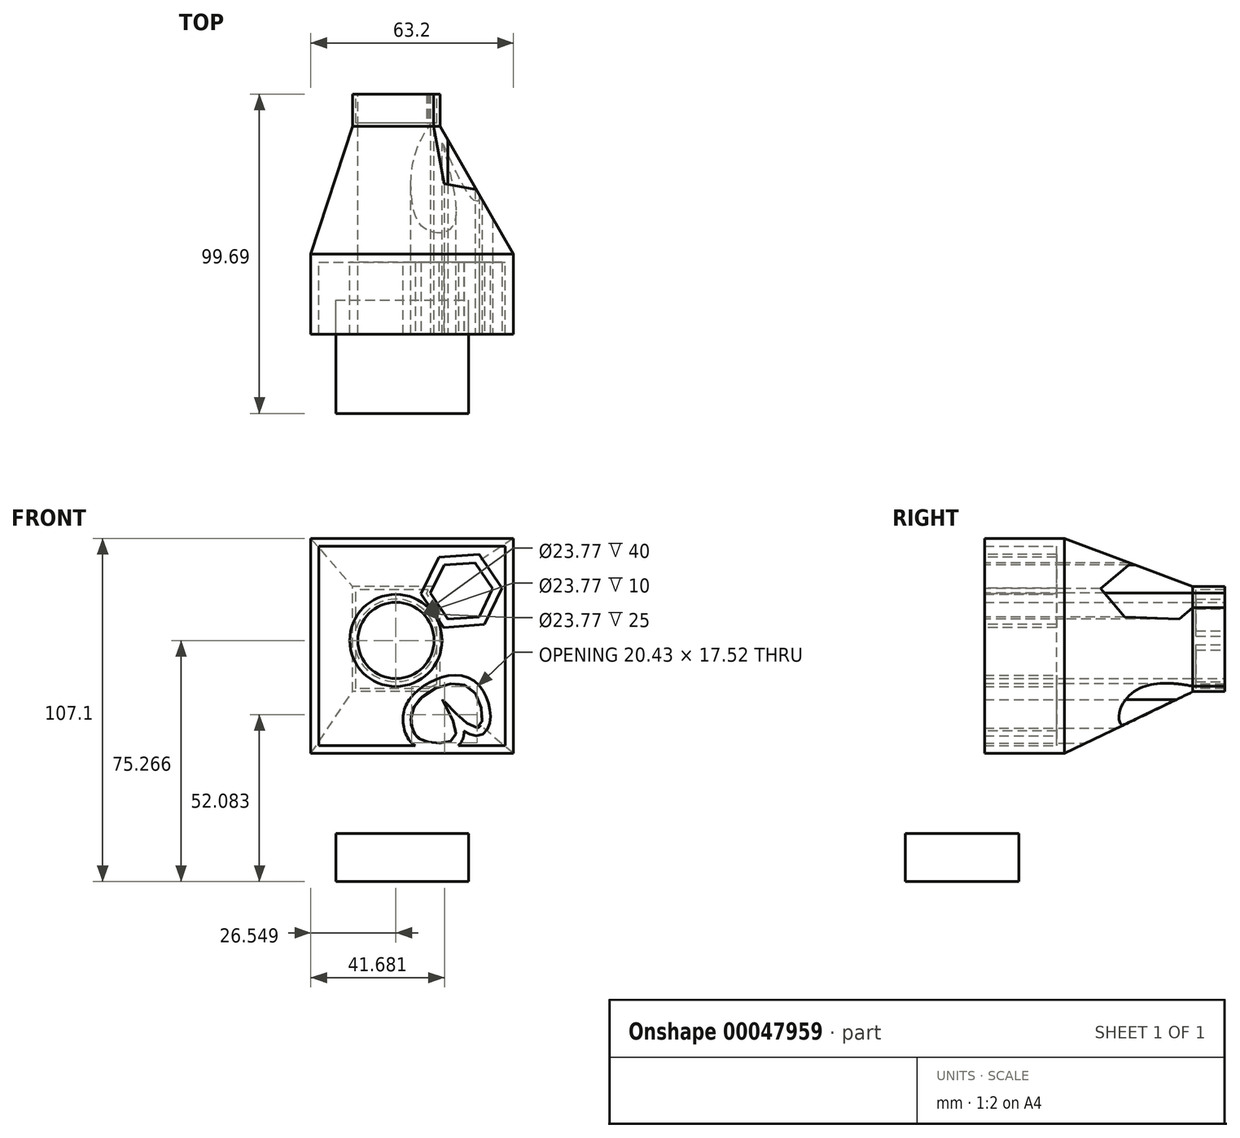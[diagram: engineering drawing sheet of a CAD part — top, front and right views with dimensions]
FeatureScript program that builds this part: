
annotation { "Feature Type Name" : "Feature", "Feature Type Description" : "" }
export const myFeature = defineFeature(function(context is Context, id is Id, definition is map)
    precondition{}
    {
        {
            var Q0;
            Q0=qCreatedBy(makeId("Front.planeOp"),FACE);
            var sketch = newSketch(context, id + "F0", { "sketchPlane" : qUnion([Q0])});
            skLineSegment(sketch, "E0.bottom", {"start": v(0, 0) * mm, "end": v(63.2, 0) * mm});
            skLineSegment(sketch, "E0.top", {"start": v(0, 67.1) * mm, "end": v(63.2, 67.1) * mm});
            skLineSegment(sketch, "E0.right", {"start": v(63.2, 0) * mm, "end": v(63.2, 67.1) * mm});
            skLineSegment(sketch, "E1", {"start": v(0, 67.1) * mm, "end": v(0, 0) * mm});
            skSolve(sketch);
        }
        {
            var Q0;
            Q0=makeQuery(id+"F0.imprint","IMPRINT",FACE,{"disambiguationData":[TD([[makeQuery(id+"F0.imprint","IMPRINT",EDGE,{"derivedFrom":sQuery(id+"F0.wireOp",EDGE,"E0.bottom")}),1.0]])]});
            extrude(context, id + "F1", {"entities" : qUnion([Q0]), "depth" : 25 * mm});
        }
        {
            var Q0;
            Q0=qCreatedBy(makeId("Front.planeOp"),FACE);
            cPlane(context, id + "F2", {"entities" : qUnion([Q0]), "cplaneType" : CPlaneType.OFFSET, "offset" : 50 * mm, "oppositeDirection" : true, "width" : 150 * mm, "height" : 150 * mm});
        }
        {
            var Q0;
            Q0=qCreatedBy(id+"F2.planeOp",FACE);
            var sketch = newSketch(context, id + "F3", { "sketchPlane" : qUnion([Q0])});
            skLineSegment(sketch, "E2.bottom", {"start": v(40.36, 19.28) * mm, "end": v(13, 19.28) * mm});
            skLineSegment(sketch, "E2.top", {"start": v(40.36, 52.07) * mm, "end": v(13, 52.07) * mm});
            skLineSegment(sketch, "E2.right", {"start": v(13, 19.28) * mm, "end": v(13, 52.07) * mm});
            skLineSegment(sketch, "E3", {"start": v(40.36, 19.28) * mm, "end": v(40.36, 52.07) * mm});
            skSolve(sketch);
        }
        {
            var Q0;
            Q0=makeQuery(id+"F3.imprint","IMPRINT",FACE,{"disambiguationData":[TD([[makeQuery(id+"F3.imprint","IMPRINT",EDGE,{"derivedFrom":sQuery(id+"F3.wireOp",EDGE,"E2.bottom")}),-1.0]])]});
            extrude(context, id + "F4", {"entities" : qUnion([Q0]), "depth" : 10 * mm});
        }
        {
            var Q0;
            Q0=makeQuery(id+"F1.opExtrude","CAP_FACE",FACE,{"disambiguationData":[OSD([sQuery(id+"F0.wireOp",EDGE,"E0.bottom"),sQuery(id+"F0.wireOp",EDGE,"E0.top"),sQuery(id+"F0.wireOp",EDGE,"E0.right"),sQuery(id+"F0.wireOp",EDGE,"E1")])],"isStart":true});
            var Q1;
            Q1=makeQuery(id+"F4.opExtrude","CAP_FACE",FACE,{"disambiguationData":[OSD([sQuery(id+"F3.wireOp",EDGE,"E2.bottom"),sQuery(id+"F3.wireOp",EDGE,"E2.top"),sQuery(id+"F3.wireOp",EDGE,"E2.right"),sQuery(id+"F3.wireOp",EDGE,"E3")])],"isStart":false});
            loft(context, id + "F5", {"sheetProfilesArray" : [{ "sheetProfileEntities" : qUnion([Q0]) }, { "sheetProfileEntities" : qUnion([Q1]) }]});
        }
        {
            var Q0;
            Q0=makeQuery(id+"F4.opExtrude","CAP_FACE",FACE,{"disambiguationData":[OSD([sQuery(id+"F3.wireOp",EDGE,"E2.bottom"),sQuery(id+"F3.wireOp",EDGE,"E2.top"),sQuery(id+"F3.wireOp",EDGE,"E2.right"),sQuery(id+"F3.wireOp",EDGE,"E3")])],"isStart":true});
            var sketch = newSketch(context, id + "F6", { "sketchPlane" : qUnion([Q0])});
            skCircle(sketch, "E4", {"center": v(-26.55, 35.27) * mm, "radius": 11.89 * mm});
            skSolve(sketch);
        }
        {
            var Q0;
            Q0=makeQuery(id+"F6.imprint","IMPRINT",FACE,{"disambiguationData":[TD([[makeQuery(id+"F6.imprint","IMPRINT",EDGE,{"derivedFrom":sQuery(id+"F6.wireOp",EDGE,"E4")}),1.0]])]});
            extrude(context, id + "F7", {"entities" : qUnion([Q0]), "operationType" : NewBodyOperationType.REMOVE, "oppositeDirection" : true, "depth" : 200 * mm});
        }
        {
            var Q0;
            Q0=makeQuery(id+"F1.opExtrude","CAP_FACE",FACE,{"disambiguationData":[OSD([sQuery(id+"F0.wireOp",EDGE,"E0.bottom"),sQuery(id+"F0.wireOp",EDGE,"E0.top"),sQuery(id+"F0.wireOp",EDGE,"E0.right"),sQuery(id+"F0.wireOp",EDGE,"E1")])],"isStart":false});
            var sketch = newSketch(context, id + "F8", { "sketchPlane" : qUnion([Q0])});
            skCircle(sketch, "E5.cCircle", {"center": v(47.04, 50.7) * mm, "radius": 8.47 * mm, "construction": true});
            skLineSegment(sketch, "E5.0", {"start": v(51.3, 59.5) * mm, "end": v(56.79, 51.41) * mm});
            skLineSegment(sketch, "E5.1", {"start": v(56.79, 51.41) * mm, "end": v(52.52, 42.62) * mm});
            skLineSegment(sketch, "E5.2", {"start": v(52.52, 42.62) * mm, "end": v(42.77, 41.91) * mm});
            skLineSegment(sketch, "E5.3", {"start": v(42.77, 41.91) * mm, "end": v(37.28, 50) * mm});
            skLineSegment(sketch, "E5.4", {"start": v(37.28, 50) * mm, "end": v(41.55, 58.8) * mm});
            skLineSegment(sketch, "E5.5", {"start": v(41.55, 58.8) * mm, "end": v(51.3, 59.5) * mm});
            skPoint(sketch, "E5.0.midPoint", {"position": v(54.05, 55.46) * mm});
            skFitSpline(sketch, "E6", {"points": [v(51.9, 7.97) * mm, v(49.75, 20.4) * mm, v(32.9, 15.55) * mm, v(32.11, 6.73) * mm, v(36.3, 3.67) * mm, v(45.23, 5.82) * mm, v(41.04, 16.8) * mm, v(51.9, 7.97) * mm]});
            skSolve(sketch);
        }
        {
            var Q0;
            Q0=makeQuery(id+"F8.imprint","IMPRINT",FACE,{"disambiguationData":[TD([[makeQuery(id+"F8.imprint","IMPRINT",EDGE,{"derivedFrom":sQuery(id+"F8.wireOp",EDGE,"E5.0")}),-1.0]])]});
            var Q1;
            Q1=makeQuery(id+"F8.imprint","IMPRINT",FACE,{"disambiguationData":[TD([[makeQuery(id+"F8.imprint","IMPRINT",EDGE,{"derivedFrom":sQuery(id+"F8.wireOp",EDGE,"E6")}),1.0]])]});
            extrude(context, id + "F9", {"entities" : qUnion([Q0, Q1]), "operationType" : NewBodyOperationType.REMOVE, "oppositeDirection" : true, "depth" : 200 * mm});
        }
        {
            var Q0;
            Q0=makeQuery(id+"F1.opExtrude","CAP_FACE",FACE,{"disambiguationData":[OSD([sQuery(id+"F0.wireOp",EDGE,"E0.bottom"),sQuery(id+"F0.wireOp",EDGE,"E0.top"),sQuery(id+"F0.wireOp",EDGE,"E0.right"),sQuery(id+"F0.wireOp",EDGE,"E1")])],"isStart":false});
            shell(context, id + "F10", {"entities" : qUnion([Q0]), "thickness" : 2.5 * mm});
        }
        {
            var Q0;
            Q0=makeQuery(id+"F4.opExtrude","CAP_FACE",FACE,{"disambiguationData":[OSD([sQuery(id+"F3.wireOp",EDGE,"E2.bottom"),sQuery(id+"F3.wireOp",EDGE,"E2.top"),sQuery(id+"F3.wireOp",EDGE,"E2.right"),sQuery(id+"F3.wireOp",EDGE,"E3")])],"isStart":true});
            shell(context, id + "F11", {"entities" : qUnion([Q0]), "thickness" : 1 * mm});
        }
        {
            var Q0;
            Q0=qCreatedBy(makeId("Top.planeOp"),FACE);
            cPlane(context, id + "F12", {"entities" : qUnion([Q0]), "cplaneType" : CPlaneType.OFFSET, "offset" : 40 * mm, "oppositeDirection" : true, "width" : 150 * mm, "height" : 150 * mm});
        }
        {
            var Q0;
            Q0=qCreatedBy(id+"F12.planeOp",FACE);
            var sketch = newSketch(context, id + "F13", { "sketchPlane" : qUnion([Q0])});
            skLineSegment(sketch, "E7.bottom", {"start": v(7.8, -49.7) * mm, "end": v(49.18, -49.7) * mm});
            skLineSegment(sketch, "E7.top", {"start": v(7.8, -14.3) * mm, "end": v(49.18, -14.3) * mm});
            skLineSegment(sketch, "E7.left", {"start": v(7.8, -49.7) * mm, "end": v(7.8, -14.3) * mm});
            skLineSegment(sketch, "E7.right", {"start": v(49.18, -49.7) * mm, "end": v(49.18, -14.3) * mm});
            skSolve(sketch);
        }
        {
            var Q0;
            Q0=makeQuery(id+"F13.imprint","IMPRINT",FACE,{"disambiguationData":[TD([[makeQuery(id+"F13.imprint","IMPRINT",EDGE,{"derivedFrom":sQuery(id+"F13.wireOp",EDGE,"E7.bottom")}),1.0]])]});
            extrude(context, id + "F14", {"entities" : qUnion([Q0]), "depth" : 15 * mm});
        }
    });
